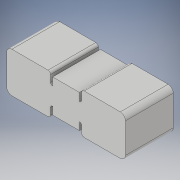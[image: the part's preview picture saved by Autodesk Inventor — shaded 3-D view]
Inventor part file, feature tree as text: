
AUTODESK INVENTOR PART (.ipt)
format: ipt  version: 2017 (Build 210142000, 142)  size: 137,216 bytes
history: native  units: in
note: dims shown in document units (in); Inventor stores cm internally (conversion verified against a paired STEP export)
features: extrude x1, sketch x1
ambient origin geometry x8: Origin, YZ Plane, XZ Plane, XY Plane, X Axis, Y Axis, Z Axis, Center Point
bodies: Solid1 (feature_tree)
feature tree (2):
  extrude  "Extrusion1"  Depth=0.85in
  sketch  "Sketch1"  dims[d1=0.39in d2=0.85in d3=0.22in d4=0.04in d5=0.32in d6=0.1in d7=0.05in d8=0.04in d9=0.926in d10=0.0in]
